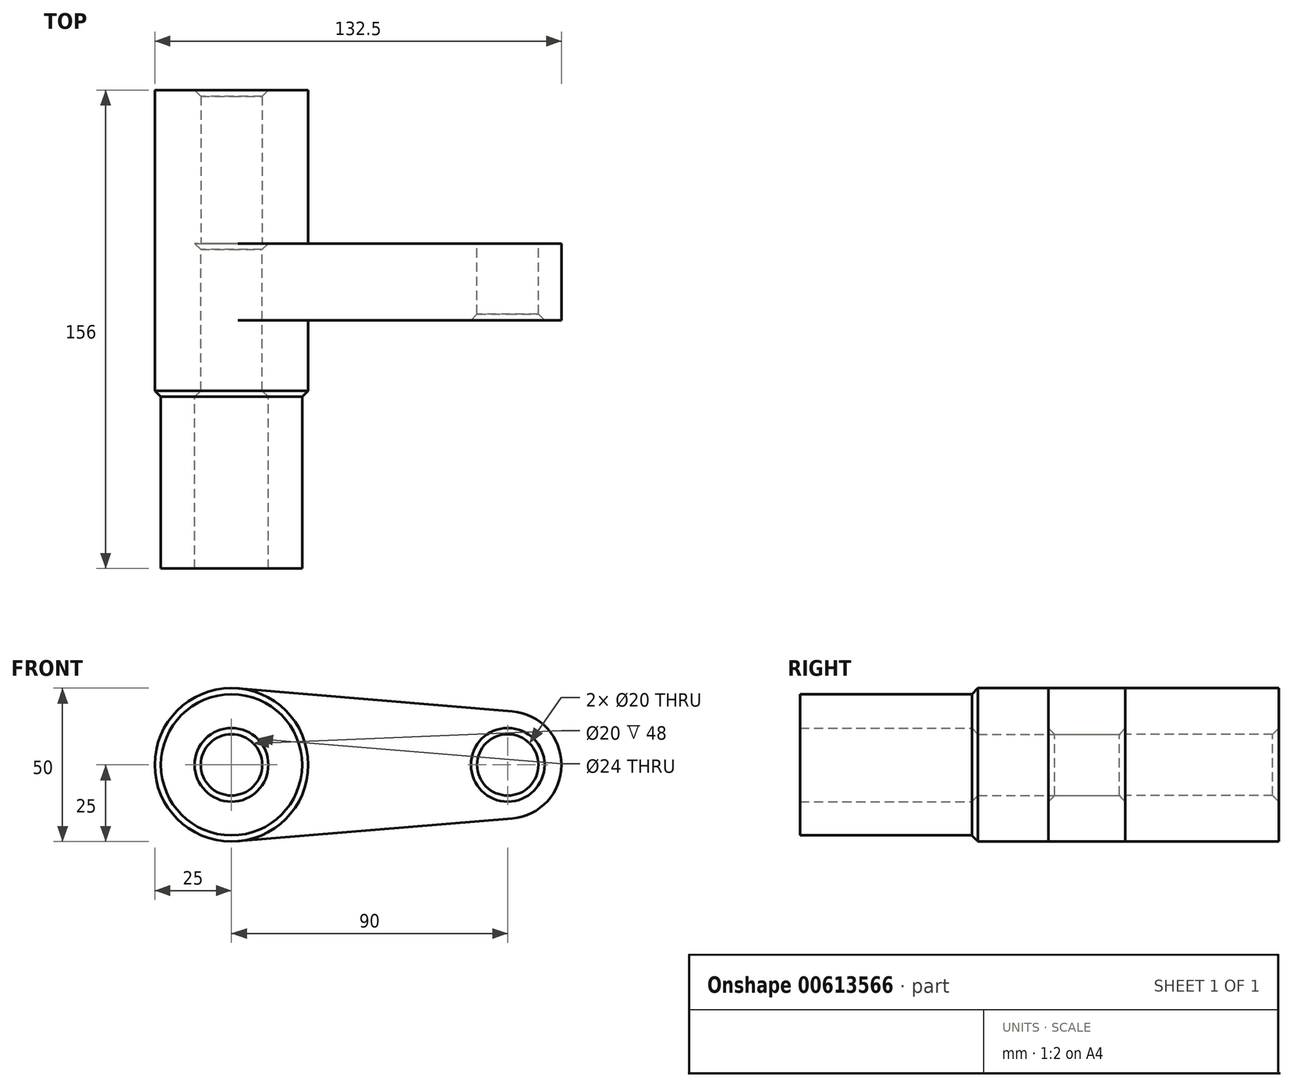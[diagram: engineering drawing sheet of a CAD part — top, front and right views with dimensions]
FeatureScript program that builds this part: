
annotation { "Feature Type Name" : "Feature", "Feature Type Description" : "" }
export const myFeature = defineFeature(function(context is Context, id is Id, definition is map)
    precondition{}
    {
        {
            var Q0;
            Q0=qCreatedBy(makeId("Front.planeOp"),FACE);
            var sketch = newSketch(context, id + "F0", { "sketchPlane" : qUnion([Q0])});
            skCircle(sketch, "E0", {"center": v(0, 0) * mm, "radius": 25 * mm});
            skCircle(sketch, "E1", {"center": v(90, 0) * mm, "radius": 17.5 * mm});
            skLineSegment(sketch, "E2", {"start": v(2.08, 24.91) * mm, "end": v(91.46, 17.44) * mm});
            skLineSegment(sketch, "E3", {"start": v(2.08, -24.91) * mm, "end": v(91.46, -17.44) * mm});
            skCircle(sketch, "E4", {"center": v(0, 0) * mm, "radius": 10 * mm});
            skCircle(sketch, "E5", {"center": v(90, 0) * mm, "radius": 10 * mm});
            skSolve(sketch);
        }
        {
            var Q0;
            Q0=qSketchRegion(id+"F0",true);
            extrude(context, id + "F1", {"entities" : qUnion([Q0]), "depth" : 25 * mm});
        }
        {
            var Q0;
            Q0=makeQuery(id+"F0.imprint","IMPRINT",FACE,{"disambiguationData":[TD([[makeQuery(id+"F0.imprint","IMPRINT",EDGE,{"derivedFrom":sQuery(id+"F0.wireOp",EDGE,"E4")}),-1.0]])]});
            extrude(context, id + "F2", {"entities" : qUnion([Q0]), "operationType" : NewBodyOperationType.ADD, "depth" : 50 * mm});
        }
        {
            var Q0;
            Q0=makeQuery(id+"F2.opExtrude","CAP_EDGE",EDGE,{"disambiguationData":[OSD([sQuery(id+"F0.wireOp",EDGE,"E0")])],"isStart":false});
            var Q1;
            Q1=makeQuery(id+"F2.opExtrude","CAP_EDGE",EDGE,{"disambiguationData":[OSD([sQuery(id+"F0.wireOp",EDGE,"E4")])],"isStart":false});
            var Q2;
            Q2=makeQuery(id+"F1.opExtrude","CAP_EDGE",EDGE,{"disambiguationData":[OSD([sQuery(id+"F0.wireOp",EDGE,"E5")])],"isStart":false});
            chamfer(context, id + "F3", {"entities" : qUnion([Q0, Q1, Q2]), "width" : 2 * mm, "tangentPropagation" : true});
        }
        {
            var Q0;
            Q0=makeQuery(id+"F1.opExtrude","CAP_EDGE",EDGE,{"disambiguationData":[OSD([sQuery(id+"F0.wireOp",EDGE,"E4")])],"isStart":true});
            chamfer(context, id + "F4", {"entities" : qUnion([Q0]), "width" : 2 * mm, "tangentPropagation" : true});
        }
        {
            var Q0;
            Q0=makeQuery(id+"F0.imprint","IMPRINT",FACE,{"disambiguationData":[TD([[makeQuery(id+"F0.imprint","IMPRINT",EDGE,{"derivedFrom":sQuery(id+"F0.wireOp",EDGE,"E4")}),-1.0]])]});
            extrude(context, id + "F5", {"entities" : qUnion([Q0]), "operationType" : NewBodyOperationType.ADD, "oppositeDirection" : true, "depth" : 50 * mm, "offsetDistance" : 25 * mm});
        }
        {
            var Q0;
            Q0=makeQuery(id+"F5.opExtrude","CAP_EDGE",EDGE,{"disambiguationData":[OSD([sQuery(id+"F0.wireOp",EDGE,"E4")])],"isStart":false});
            chamfer(context, id + "F6", {"entities" : qUnion([Q0]), "width" : 2 * mm, "tangentPropagation" : true});
        }
        {
            var Q0;
            Q0=makeQuery(id+"F2.opExtrude","CAP_FACE",FACE,{"disambiguationData":[OSD([sQuery(id+"F0.wireOp",EDGE,"E0"),sQuery(id+"F0.wireOp",EDGE,"E4")])],"isStart":false});
            extrude(context, id + "F7", {"entities" : qUnion([Q0]), "operationType" : NewBodyOperationType.ADD, "depth" : 56 * mm, "offsetDistance" : 25 * mm});
        }
    });
